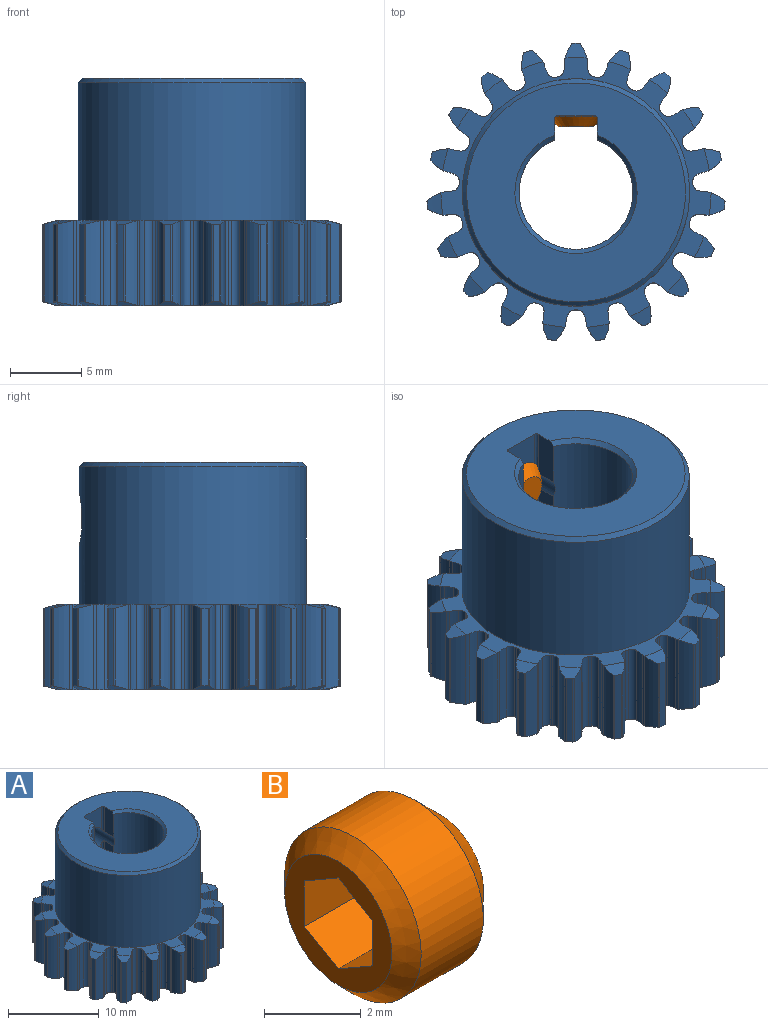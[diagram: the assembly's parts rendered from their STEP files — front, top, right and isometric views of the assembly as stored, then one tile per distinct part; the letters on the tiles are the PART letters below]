
ASSEMBLY  parts=2 mates=1
PART A: 286 faces, bbox 21x21x16 mm
  f0: plane 3.39x1.5mm, normal (-1,0,0), area 5mm2, adj f1,f3,f13,f14,f197
  f1: cone r=4mm half-angle=45deg, axis (0,0,1), area 9.8mm2, adj f0,f13,f14,f199
  f2: cylinder r=0.2mm len=11.39mm, axis (0,0,1), area 3.5mm2, adj f3,f11,f194,f200
  f3: cylinder r=1.62mm len=3.91mm, axis (0,-1,0), area 27mm2, adj f0,f2,f14,f194,f195,f196,f197,f198
  f4: cylinder r=3.17mm len=6mm, axis (0,0,1), area 6.3mm2, adj f5,f6,f150,f192
  f5: cylinder r=0.1mm len=5.49mm, axis (0,0,1), area 0.5mm2, adj f4,f6,f192,f250
  f6: cone r=9.5mm half-angle=75deg, axis (0,0,-1), area 1.1mm2, adj f4,f5,f10,f16,f250,f285
  f7: cylinder r=0.1mm len=5.49mm, axis (0,0,1), area 0.5mm2, adj f193,f221,f227,f242
  f8: cylinder r=3.17mm len=6mm, axis (0,0,1), area 6.3mm2, adj f9,f193,f221,f243
  f9: cylinder r=0.1mm len=5.49mm, axis (0,0,1), area 0.5mm2, adj f8,f193,f221,f227
  f10: cylinder r=0.1mm len=5.49mm, axis (0,0,1), area 0.5mm2, adj f6,f16,f192,f250
  f11: plane 19x18.97mm, normal (0,0,-1), area 192.8mm2, adj f2,f12,f18,f19,f20,f21,f22,f23
  f12: cone r=4.3mm half-angle=45deg, axis (0,0,-1), area 9.8mm2, adj f11,f14,f200,f201
  f13: plane 15.4x15.4mm, normal (0,0,1), area 124.6mm2, adj f0,f1,f196,f197,f199,f202,f203
  f14: cylinder r=4mm len=15.4mm, axis (0,0,1), area 339.5mm2, adj f0,f1,f3,f12,f199,f200,f201
  f15: cylinder r=8mm len=16mm, axis (0,0,1), area 476.3mm2, adj f195,f203,f285
  f16: cylinder r=3.17mm len=6mm, axis (0,0,1), area 6.3mm2, adj f6,f10,f192,f249
  f17: cylinder r=3.17mm len=6mm, axis (0,0,1), area 6.3mm2, adj f18,f153,f169,f218
  f18: cylinder r=0.81mm len=6mm, axis (0,0,1), area 1.6mm2, adj f11,f17,f19,f285
  f19: cylinder r=2.92mm len=6mm, axis (0,0,1), area 3.9mm2, adj f11,f18,f20,f285
  f20: cylinder r=0.5mm len=6mm, axis (0,0,1), area 3.7mm2, adj f11,f19,f21,f285
  f21: cylinder r=8.25mm len=6mm, axis (0,0,1), area 1.1mm2, adj f11,f20,f22,f285
  f22: cylinder r=0.5mm len=6mm, axis (0,0,1), area 3.7mm2, adj f11,f21,f23,f285
  f23: cylinder r=2.92mm len=6mm, axis (0,0,1), area 3.9mm2, adj f11,f22,f24,f285
  f24: cylinder r=0.81mm len=6mm, axis (0,0,1), area 1.6mm2, adj f11,f23,f25,f285
  f25: cylinder r=3.17mm len=6mm, axis (0,0,1), area 6.3mm2, adj f24,f170,f178,f217
  f26: cylinder r=3.17mm len=6mm, axis (0,0,1), area 6.3mm2, adj f27,f170,f176,f217
  f27: cylinder r=0.81mm len=6mm, axis (0,0,1), area 1.6mm2, adj f11,f26,f28,f285
  f28: cylinder r=2.92mm len=6mm, axis (0,0,1), area 3.9mm2, adj f11,f27,f29,f285
  f29: cylinder r=0.5mm len=6mm, axis (0,0,1), area 3.7mm2, adj f11,f28,f30,f285
  f30: cylinder r=8.25mm len=6mm, axis (0,0,1), area 1.1mm2, adj f11,f29,f31,f285
  f31: cylinder r=0.5mm len=6mm, axis (0,0,1), area 3.7mm2, adj f11,f30,f32,f285
  f32: cylinder r=2.92mm len=6mm, axis (0,0,1), area 3.9mm2, adj f11,f31,f33,f285
  f33: cylinder r=0.81mm len=6mm, axis (0,0,1), area 1.6mm2, adj f11,f32,f34,f285
  f34: cylinder r=3.17mm len=6mm, axis (0,0,1), area 6.3mm2, adj f33,f171,f175,f216
  f35: cylinder r=3.17mm len=6mm, axis (0,0,1), area 6.3mm2, adj f36,f171,f172,f216
  f36: cylinder r=0.81mm len=6mm, axis (0,0,1), area 1.6mm2, adj f11,f35,f37,f285
  f37: cylinder r=2.92mm len=6mm, axis (0,0,1), area 3.9mm2, adj f11,f36,f38,f285
  f38: cylinder r=0.5mm len=6mm, axis (0,0,1), area 3.7mm2, adj f11,f37,f39,f285
  f39: cylinder r=8.25mm len=6mm, axis (0,0,1), area 1.1mm2, adj f11,f38,f40,f285
  f40: cylinder r=0.5mm len=6mm, axis (0,0,1), area 3.7mm2, adj f11,f39,f41,f285
  f41: cylinder r=2.92mm len=6mm, axis (0,0,1), area 3.9mm2, adj f11,f40,f42,f285
  f42: cylinder r=0.81mm len=6mm, axis (0,0,1), area 1.6mm2, adj f11,f41,f43,f285
  f43: cylinder r=3.17mm len=6mm, axis (0,0,1), area 6.3mm2, adj f42,f173,f181,f215
  f44: cylinder r=3.17mm len=6mm, axis (0,0,1), area 6.3mm2, adj f45,f181,f215,f284
  f45: cylinder r=0.81mm len=6mm, axis (0,0,1), area 1.6mm2, adj f11,f44,f46,f285
  f46: cylinder r=2.92mm len=6mm, axis (0,0,1), area 3.9mm2, adj f11,f45,f47,f285
  f47: cylinder r=0.5mm len=6mm, axis (0,0,1), area 3.7mm2, adj f11,f46,f48,f285
  f48: cylinder r=8.25mm len=6mm, axis (0,0,1), area 1.1mm2, adj f11,f47,f49,f285
  f49: cylinder r=0.5mm len=6mm, axis (0,0,1), area 3.7mm2, adj f11,f48,f50,f285
  f50: cylinder r=2.92mm len=6mm, axis (0,0,1), area 3.9mm2, adj f11,f49,f51,f285
  f51: cylinder r=0.81mm len=6mm, axis (0,0,1), area 1.6mm2, adj f11,f50,f52,f285
  f52: cylinder r=3.17mm len=6mm, axis (0,0,1), area 6.3mm2, adj f51,f180,f214,f283
  f53: cylinder r=3.17mm len=6mm, axis (0,0,1), area 6.3mm2, adj f54,f180,f214,f281
  f54: cylinder r=0.81mm len=6mm, axis (0,0,1), area 1.6mm2, adj f11,f53,f55,f285
  f55: cylinder r=2.92mm len=6mm, axis (0,0,1), area 3.9mm2, adj f11,f54,f56,f285
  f56: cylinder r=0.5mm len=6mm, axis (0,0,1), area 3.7mm2, adj f11,f55,f57,f285
  f57: cylinder r=8.25mm len=6mm, axis (0,0,1), area 1.1mm2, adj f11,f56,f58,f285
  f58: cylinder r=0.5mm len=6mm, axis (0,0,1), area 3.7mm2, adj f11,f57,f59,f285
  f59: cylinder r=2.92mm len=6mm, axis (0,0,1), area 3.9mm2, adj f11,f58,f60,f285
  f60: cylinder r=0.81mm len=6mm, axis (0,0,1), area 1.6mm2, adj f11,f59,f61,f285
  f61: cylinder r=3.17mm len=6mm, axis (0,0,1), area 6.3mm2, adj f60,f182,f213,f280
  f62: cylinder r=3.17mm len=6mm, axis (0,0,1), area 6.3mm2, adj f63,f182,f213,f278
  f63: cylinder r=0.81mm len=6mm, axis (0,0,1), area 1.6mm2, adj f11,f62,f64,f285
  f64: cylinder r=2.92mm len=6mm, axis (0,0,1), area 3.9mm2, adj f11,f63,f65,f285
  f65: cylinder r=0.5mm len=6mm, axis (0,0,1), area 3.7mm2, adj f11,f64,f66,f285
  f66: cylinder r=8.25mm len=6mm, axis (0,0,1), area 1.1mm2, adj f11,f65,f67,f285
  f67: cylinder r=0.5mm len=6mm, axis (0,0,1), area 3.7mm2, adj f11,f66,f68,f285
  f68: cylinder r=2.92mm len=6mm, axis (0,0,1), area 3.9mm2, adj f11,f67,f69,f285
  f69: cylinder r=0.81mm len=6mm, axis (0,0,1), area 1.6mm2, adj f11,f68,f70,f285
  f70: cylinder r=3.17mm len=6mm, axis (0,0,1), area 6.3mm2, adj f69,f183,f212,f277
  f71: cylinder r=3.17mm len=6mm, axis (0,0,1), area 6.3mm2, adj f72,f183,f212,f275
  f72: cylinder r=0.81mm len=6mm, axis (0,0,1), area 1.6mm2, adj f11,f71,f73,f285
  f73: cylinder r=2.92mm len=6mm, axis (0,0,1), area 3.9mm2, adj f11,f72,f74,f285
  f74: cylinder r=0.5mm len=6mm, axis (0,0,1), area 3.7mm2, adj f11,f73,f75,f285
  f75: cylinder r=8.25mm len=6mm, axis (0,0,1), area 1.1mm2, adj f11,f74,f76,f285
  f76: cylinder r=0.5mm len=6mm, axis (0,0,1), area 3.7mm2, adj f11,f75,f77,f285
  f77: cylinder r=2.92mm len=6mm, axis (0,0,1), area 3.9mm2, adj f11,f76,f78,f285
  f78: cylinder r=0.81mm len=6mm, axis (0,0,1), area 1.6mm2, adj f11,f77,f79,f285
  f79: cylinder r=3.17mm len=6mm, axis (0,0,1), area 6.3mm2, adj f78,f184,f211,f274
  f80: cylinder r=3.17mm len=6mm, axis (0,0,1), area 6.3mm2, adj f81,f184,f211,f272
  f81: cylinder r=0.81mm len=6mm, axis (0,0,1), area 1.6mm2, adj f11,f80,f82,f285
  f82: cylinder r=2.92mm len=6mm, axis (0,0,1), area 3.9mm2, adj f11,f81,f83,f285
  f83: cylinder r=0.5mm len=6mm, axis (0,0,1), area 3.7mm2, adj f11,f82,f84,f285
  f84: cylinder r=8.25mm len=6mm, axis (0,0,1), area 1.1mm2, adj f11,f83,f85,f285
  f85: cylinder r=0.5mm len=6mm, axis (0,0,1), area 3.7mm2, adj f11,f84,f86,f285
  f86: cylinder r=2.92mm len=6mm, axis (0,0,1), area 3.9mm2, adj f11,f85,f87,f285
  f87: cylinder r=0.81mm len=6mm, axis (0,0,1), area 1.6mm2, adj f11,f86,f88,f285
  f88: cylinder r=3.17mm len=6mm, axis (0,0,1), area 6.3mm2, adj f87,f185,f210,f271
  f89: cylinder r=3.17mm len=6mm, axis (0,0,1), area 6.3mm2, adj f90,f185,f210,f269
  f90: cylinder r=0.81mm len=6mm, axis (0,0,1), area 1.6mm2, adj f11,f89,f91,f285
  f91: cylinder r=2.92mm len=6mm, axis (0,0,1), area 3.9mm2, adj f11,f90,f92,f285
  f92: cylinder r=0.5mm len=6mm, axis (0,0,1), area 3.7mm2, adj f11,f91,f93,f285
  f93: cylinder r=8.25mm len=6mm, axis (0,0,1), area 1.1mm2, adj f11,f92,f94,f285
  f94: cylinder r=0.5mm len=6mm, axis (0,0,1), area 3.7mm2, adj f11,f93,f95,f285
  f95: cylinder r=2.92mm len=6mm, axis (0,0,1), area 3.9mm2, adj f11,f94,f96,f285
  f96: cylinder r=0.81mm len=6mm, axis (0,0,1), area 1.6mm2, adj f11,f95,f97,f285
  f97: cylinder r=3.17mm len=6mm, axis (0,0,1), area 6.3mm2, adj f96,f186,f209,f268
  f98: cylinder r=3.17mm len=6mm, axis (0,0,1), area 6.3mm2, adj f99,f186,f209,f266
  f99: cylinder r=0.81mm len=6mm, axis (0,0,1), area 1.6mm2, adj f11,f98,f100,f285
  f100: cylinder r=2.92mm len=6mm, axis (0,0,1), area 3.9mm2, adj f11,f99,f101,f285
  f101: cylinder r=0.5mm len=6mm, axis (0,0,1), area 3.7mm2, adj f11,f100,f102,f285
  f102: cylinder r=8.25mm len=6mm, axis (0,0,1), area 1.1mm2, adj f11,f101,f103,f285
  f103: cylinder r=0.5mm len=6mm, axis (0,0,1), area 3.7mm2, adj f11,f102,f104,f285
  f104: cylinder r=2.92mm len=6mm, axis (0,0,1), area 3.9mm2, adj f11,f103,f105,f285
  f105: cylinder r=0.81mm len=6mm, axis (0,0,1), area 1.6mm2, adj f11,f104,f106,f285
  f106: cylinder r=3.17mm len=6mm, axis (0,0,1), area 6.3mm2, adj f105,f187,f208,f265
  f107: cylinder r=3.17mm len=6mm, axis (0,0,1), area 6.3mm2, adj f108,f187,f208,f263
  f108: cylinder r=0.81mm len=6mm, axis (0,0,1), area 1.6mm2, adj f11,f107,f109,f285
  f109: cylinder r=2.92mm len=6mm, axis (0,0,1), area 3.9mm2, adj f11,f108,f110,f285
  f110: cylinder r=0.5mm len=6mm, axis (0,0,1), area 3.7mm2, adj f11,f109,f111,f285
  f111: cylinder r=8.25mm len=6mm, axis (0,0,1), area 1.1mm2, adj f11,f110,f112,f285
  f112: cylinder r=0.5mm len=6mm, axis (0,0,1), area 3.7mm2, adj f11,f111,f113,f285
  f113: cylinder r=2.92mm len=6mm, axis (0,0,1), area 3.9mm2, adj f11,f112,f114,f285
  f114: cylinder r=0.81mm len=6mm, axis (0,0,1), area 1.6mm2, adj f11,f113,f115,f285
  f115: cylinder r=3.17mm len=6mm, axis (0,0,1), area 6.3mm2, adj f114,f188,f207,f262
  f116: cylinder r=3.17mm len=6mm, axis (0,0,1), area 6.3mm2, adj f117,f188,f207,f260
  f117: cylinder r=0.81mm len=6mm, axis (0,0,1), area 1.6mm2, adj f11,f116,f118,f285
  f118: cylinder r=2.92mm len=6mm, axis (0,0,1), area 3.9mm2, adj f11,f117,f119,f285
  f119: cylinder r=0.5mm len=6mm, axis (0,0,1), area 3.7mm2, adj f11,f118,f120,f285
  f120: cylinder r=8.25mm len=6mm, axis (0,0,1), area 1.1mm2, adj f11,f119,f121,f285
  f121: cylinder r=0.5mm len=6mm, axis (0,0,1), area 3.7mm2, adj f11,f120,f122,f285
  f122: cylinder r=2.92mm len=6mm, axis (0,0,1), area 3.9mm2, adj f11,f121,f123,f285
  f123: cylinder r=0.81mm len=6mm, axis (0,0,1), area 1.6mm2, adj f11,f122,f124,f285
  f124: cylinder r=3.17mm len=6mm, axis (0,0,1), area 6.3mm2, adj f123,f189,f206,f259
  f125: cylinder r=3.17mm len=6mm, axis (0,0,1), area 6.3mm2, adj f126,f189,f206,f257
  f126: cylinder r=0.81mm len=6mm, axis (0,0,1), area 1.6mm2, adj f11,f125,f127,f285
  f127: cylinder r=2.92mm len=6mm, axis (0,0,1), area 3.9mm2, adj f11,f126,f128,f285
  f128: cylinder r=0.5mm len=6mm, axis (0,0,1), area 3.7mm2, adj f11,f127,f129,f285
  f129: cylinder r=8.25mm len=6mm, axis (0,0,1), area 1.1mm2, adj f11,f128,f130,f285
  f130: cylinder r=0.5mm len=6mm, axis (0,0,1), area 3.7mm2, adj f11,f129,f131,f285
  f131: cylinder r=2.92mm len=6mm, axis (0,0,1), area 3.9mm2, adj f11,f130,f132,f285
  f132: cylinder r=0.81mm len=6mm, axis (0,0,1), area 1.6mm2, adj f11,f131,f133,f285
  f133: cylinder r=3.17mm len=6mm, axis (0,0,1), area 6.3mm2, adj f132,f190,f205,f256
  f134: cylinder r=3.17mm len=6mm, axis (0,0,1), area 6.3mm2, adj f135,f190,f205,f254
  f135: cylinder r=0.81mm len=6mm, axis (0,0,1), area 1.6mm2, adj f11,f134,f136,f285
  f136: cylinder r=2.92mm len=6mm, axis (0,0,1), area 3.9mm2, adj f11,f135,f137,f285
  f137: cylinder r=0.5mm len=6mm, axis (0,0,1), area 3.7mm2, adj f11,f136,f138,f285
  f138: cylinder r=8.25mm len=6mm, axis (0,0,1), area 1.1mm2, adj f11,f137,f139,f285
  f139: cylinder r=0.5mm len=6mm, axis (0,0,1), area 3.7mm2, adj f11,f138,f140,f285
  f140: cylinder r=2.92mm len=6mm, axis (0,0,1), area 3.9mm2, adj f11,f139,f141,f285
  f141: cylinder r=0.81mm len=6mm, axis (0,0,1), area 1.6mm2, adj f11,f140,f142,f285
  f142: cylinder r=3.17mm len=6mm, axis (0,0,1), area 6.3mm2, adj f141,f191,f204,f253
  f143: cylinder r=3.17mm len=6mm, axis (0,0,1), area 6.3mm2, adj f144,f191,f204,f251
  f144: cylinder r=0.81mm len=6mm, axis (0,0,1), area 1.6mm2, adj f11,f143,f145,f285
  f145: cylinder r=2.92mm len=6mm, axis (0,0,1), area 3.9mm2, adj f11,f144,f146,f285
  f146: cylinder r=0.5mm len=6mm, axis (0,0,1), area 3.7mm2, adj f11,f145,f147,f285
  f147: cylinder r=8.25mm len=6mm, axis (0,0,1), area 1.1mm2, adj f11,f146,f148,f285
  f148: cylinder r=0.5mm len=6mm, axis (0,0,1), area 3.7mm2, adj f11,f147,f149,f285
  f149: cylinder r=2.92mm len=6mm, axis (0,0,1), area 3.9mm2, adj f11,f148,f150,f285
  f150: cylinder r=0.81mm len=6mm, axis (0,0,1), area 1.6mm2, adj f4,f11,f149,f285
  f151: cylinder r=0.1mm len=5.49mm, axis (0,0,1), area 0.5mm2, adj f152,f162,f169,f218
  f152: cylinder r=10.5mm len=5.46mm, axis (0,0,1), area 2.6mm2, adj f151,f153,f169,f218
  f153: cylinder r=0.1mm len=5.49mm, axis (0,0,1), area 0.5mm2, adj f17,f152,f169,f218
  f154: cylinder r=3.17mm len=6mm, axis (0,0,1), area 6.3mm2, adj f155,f167,f219,f226
  f155: cylinder r=0.81mm len=6mm, axis (0,0,1), area 1.6mm2, adj f11,f154,f156,f285
  f156: cylinder r=2.92mm len=6mm, axis (0,0,1), area 3.9mm2, adj f11,f155,f157,f285
  f157: cylinder r=0.5mm len=6mm, axis (0,0,1), area 3.7mm2, adj f11,f156,f158,f285
  f158: cylinder r=8.25mm len=6mm, axis (0,0,1), area 1.1mm2, adj f11,f157,f159,f285
  f159: cylinder r=0.5mm len=6mm, axis (0,0,1), area 3.7mm2, adj f11,f158,f160,f285
  f160: cylinder r=2.92mm len=6mm, axis (0,0,1), area 3.9mm2, adj f11,f159,f161,f285
  f161: cylinder r=0.81mm len=6mm, axis (0,0,1), area 1.6mm2, adj f11,f160,f162,f285
  f162: cylinder r=3.17mm len=6mm, axis (0,0,1), area 6.3mm2, adj f151,f161,f169,f218
  f163: cylinder r=3.17mm len=6mm, axis (0,0,1), area 6.3mm2, adj f164,f167,f219,f229
  f164: cylinder r=0.1mm len=5.49mm, axis (0,0,1), area 0.5mm2, adj f163,f167,f219,f225
  f165: cylinder r=0.1mm len=5.49mm, axis (0,0,1), area 0.5mm2, adj f166,f168,f220,f224
  f166: cylinder r=3.17mm len=6mm, axis (0,0,1), area 6.3mm2, adj f165,f168,f220,f234
  f167: cone r=15.5mm half-angle=75deg, axis (0,0,1), area 1.1mm2, adj f11,f154,f163,f164,f225,f226
  f168: cone r=15.5mm half-angle=75deg, axis (0,0,1), area 1.1mm2, adj f11,f165,f166,f222,f223,f224
  f169: cone r=15.5mm half-angle=75deg, axis (0,0,1), area 1.1mm2, adj f11,f17,f151,f152,f153,f162
  f170: cone r=15.5mm half-angle=75deg, axis (0,0,1), area 1.1mm2, adj f11,f25,f26,f176,f177,f178
  f171: cone r=15.5mm half-angle=75deg, axis (0,0,1), area 1.1mm2, adj f11,f34,f35,f172,f174,f175
  f172: cylinder r=0.1mm len=5.49mm, axis (0,0,1), area 0.5mm2, adj f35,f171,f174,f216
  f173: cylinder r=0.1mm len=5.49mm, axis (0,0,1), area 0.5mm2, adj f43,f179,f181,f215
  f174: cylinder r=10.5mm len=5.46mm, axis (0,0,1), area 2.6mm2, adj f171,f172,f175,f216
  f175: cylinder r=0.1mm len=5.49mm, axis (0,0,1), area 0.5mm2, adj f34,f171,f174,f216
  f176: cylinder r=0.1mm len=5.49mm, axis (0,0,1), area 0.5mm2, adj f26,f170,f177,f217
  f177: cylinder r=10.5mm len=5.46mm, axis (0,0,1), area 2.6mm2, adj f170,f176,f178,f217
  f178: cylinder r=0.1mm len=5.49mm, axis (0,0,1), area 0.5mm2, adj f25,f170,f177,f217
  f179: cylinder r=10.5mm len=5.46mm, axis (0,0,1), area 2.6mm2, adj f173,f181,f215,f284
  f180: cone r=15.5mm half-angle=75deg, axis (0,0,1), area 1.1mm2, adj f11,f52,f53,f281,f282,f283
  f181: cone r=15.5mm half-angle=75deg, axis (0,0,1), area 1.1mm2, adj f11,f43,f44,f173,f179,f284
  f182: cone r=15.5mm half-angle=75deg, axis (0,0,1), area 1.1mm2, adj f11,f61,f62,f278,f279,f280
  f183: cone r=15.5mm half-angle=75deg, axis (0,0,1), area 1.1mm2, adj f11,f70,f71,f275,f276,f277
  f184: cone r=15.5mm half-angle=75deg, axis (0,0,1), area 1.1mm2, adj f11,f79,f80,f272,f273,f274
  f185: cone r=15.5mm half-angle=75deg, axis (0,0,1), area 1.1mm2, adj f11,f88,f89,f269,f270,f271
  f186: cone r=15.5mm half-angle=75deg, axis (0,0,1), area 1.1mm2, adj f11,f97,f98,f266,f267,f268
  f187: cone r=15.5mm half-angle=75deg, axis (0,0,1), area 1.1mm2, adj f11,f106,f107,f263,f264,f265
  f188: cone r=15.5mm half-angle=75deg, axis (0,0,1), area 1.1mm2, adj f11,f115,f116,f260,f261,f262
  f189: cone r=15.5mm half-angle=75deg, axis (0,0,1), area 1.1mm2, adj f11,f124,f125,f257,f258,f259
  f190: cone r=15.5mm half-angle=75deg, axis (0,0,1), area 1.1mm2, adj f11,f133,f134,f254,f255,f256
  f191: cone r=15.5mm half-angle=75deg, axis (0,0,1), area 1.1mm2, adj f11,f142,f143,f251,f252,f253
  f192: cone r=15.5mm half-angle=75deg, axis (0,0,1), area 1.1mm2, adj f4,f5,f10,f11,f16,f250
  f193: cone r=15.5mm half-angle=75deg, axis (0,0,1), area 1.1mm2, adj f7,f8,f9,f11,f227,f242
  f194: plane 11.03x2.6mm, normal (0,-1,0), area 27.5mm2, adj f2,f3,f11,f198
  f195: cone r=1.62mm half-angle=45deg, axis (0,1,0), area 5.1mm2, adj f3,f15
  f196: plane 3.03x2.6mm, normal (0,-1,0), area 6.7mm2, adj f3,f13,f197,f202
  f197: cylinder r=0.2mm len=3.39mm, axis (0,0,1), area 1mm2, adj f0,f3,f13,f196
  f198: cylinder r=0.2mm len=11.39mm, axis (0,0,1), area 3.5mm2, adj f3,f11,f194,f201
  f199: plane 3.39x1.5mm, normal (1,0,0), area 5mm2, adj f1,f3,f13,f14,f202
  f200: plane 11.39x1.5mm, normal (1,0,0), area 16.9mm2, adj f2,f3,f11,f12,f14
  f201: plane 11.39x1.5mm, normal (-1,0,0), area 16.9mm2, adj f3,f11,f12,f14,f198
  f202: cylinder r=0.2mm len=3.39mm, axis (0,0,1), area 1mm2, adj f3,f13,f196,f199
  f203: cone r=7.7mm half-angle=45deg, axis (0,0,-1), area 20.9mm2, adj f13,f15
  f204: cone r=9.5mm half-angle=75deg, axis (0,0,-1), area 1.1mm2, adj f142,f143,f251,f252,f253,f285
  f205: cone r=9.5mm half-angle=75deg, axis (0,0,-1), area 1.1mm2, adj f133,f134,f254,f255,f256,f285
  f206: cone r=9.5mm half-angle=75deg, axis (0,0,-1), area 1.1mm2, adj f124,f125,f257,f258,f259,f285
  f207: cone r=9.5mm half-angle=75deg, axis (0,0,-1), area 1.1mm2, adj f115,f116,f260,f261,f262,f285
  f208: cone r=9.5mm half-angle=75deg, axis (0,0,-1), area 1.1mm2, adj f106,f107,f263,f264,f265,f285
  f209: cone r=9.5mm half-angle=75deg, axis (0,0,-1), area 1.1mm2, adj f97,f98,f266,f267,f268,f285
  f210: cone r=9.5mm half-angle=75deg, axis (0,0,-1), area 1.1mm2, adj f88,f89,f269,f270,f271,f285
  f211: cone r=9.5mm half-angle=75deg, axis (0,0,-1), area 1.1mm2, adj f79,f80,f272,f273,f274,f285
  f212: cone r=9.5mm half-angle=75deg, axis (0,0,-1), area 1.1mm2, adj f70,f71,f275,f276,f277,f285
  f213: cone r=9.5mm half-angle=75deg, axis (0,0,-1), area 1.1mm2, adj f61,f62,f278,f279,f280,f285
  f214: cone r=9.5mm half-angle=75deg, axis (0,0,-1), area 1.1mm2, adj f52,f53,f281,f282,f283,f285
  f215: cone r=9.5mm half-angle=75deg, axis (0,0,-1), area 1.1mm2, adj f43,f44,f173,f179,f284,f285
  f216: cone r=9.5mm half-angle=75deg, axis (0,0,-1), area 1.1mm2, adj f34,f35,f172,f174,f175,f285
  f217: cone r=9.5mm half-angle=75deg, axis (0,0,-1), area 1.1mm2, adj f25,f26,f176,f177,f178,f285
  f218: cone r=9.5mm half-angle=75deg, axis (0,0,-1), area 1.1mm2, adj f17,f151,f152,f153,f162,f285
  f219: cone r=9.5mm half-angle=75deg, axis (0,0,-1), area 1.1mm2, adj f154,f163,f164,f225,f226,f285
  f220: cone r=9.5mm half-angle=75deg, axis (0,0,-1), area 1.1mm2, adj f165,f166,f222,f223,f224,f285
  f221: cone r=9.5mm half-angle=75deg, axis (0,0,-1), area 1.1mm2, adj f7,f8,f9,f227,f242,f285
  f222: cylinder r=3.17mm len=6mm, axis (0,0,1), area 6.3mm2, adj f168,f220,f223,f235
  f223: cylinder r=0.1mm len=5.49mm, axis (0,0,1), area 0.5mm2, adj f168,f220,f222,f224
  f224: cylinder r=10.5mm len=5.46mm, axis (0,0,1), area 2.6mm2, adj f165,f168,f220,f223
  f225: cylinder r=10.5mm len=5.46mm, axis (0,0,1), area 2.6mm2, adj f164,f167,f219,f226
  f226: cylinder r=0.1mm len=5.49mm, axis (0,0,1), area 0.5mm2, adj f154,f167,f219,f225
  f227: cylinder r=10.5mm len=5.46mm, axis (0,0,1), area 2.6mm2, adj f7,f9,f193,f221
  f228: cylinder r=2.92mm len=6mm, axis (0,0,1), area 3.9mm2, adj f11,f229,f230,f285
  f229: cylinder r=0.81mm len=6mm, axis (0,0,1), area 1.6mm2, adj f11,f163,f228,f285
  f230: cylinder r=0.5mm len=6mm, axis (0,0,1), area 3.7mm2, adj f11,f228,f231,f285
  f231: cylinder r=8.25mm len=6mm, axis (0,0,1), area 1.1mm2, adj f11,f230,f232,f285
  f232: cylinder r=0.5mm len=6mm, axis (0,0,1), area 3.7mm2, adj f11,f231,f233,f285
  f233: cylinder r=2.92mm len=6mm, axis (0,0,1), area 3.9mm2, adj f11,f232,f234,f285
  f234: cylinder r=0.81mm len=6mm, axis (0,0,1), area 1.6mm2, adj f11,f166,f233,f285
  f235: cylinder r=0.81mm len=6mm, axis (0,0,1), area 1.6mm2, adj f11,f222,f236,f285
  f236: cylinder r=2.92mm len=6mm, axis (0,0,1), area 3.9mm2, adj f11,f235,f237,f285
  f237: cylinder r=0.5mm len=6mm, axis (0,0,1), area 3.7mm2, adj f11,f236,f238,f285
  f238: cylinder r=8.25mm len=6mm, axis (0,0,1), area 1.1mm2, adj f11,f237,f239,f285
  f239: cylinder r=0.5mm len=6mm, axis (0,0,1), area 3.7mm2, adj f11,f238,f240,f285
  f240: cylinder r=2.92mm len=6mm, axis (0,0,1), area 3.9mm2, adj f11,f239,f241,f285
  f241: cylinder r=0.81mm len=6mm, axis (0,0,1), area 1.6mm2, adj f11,f240,f242,f285
  f242: cylinder r=3.17mm len=6mm, axis (0,0,1), area 6.3mm2, adj f7,f193,f221,f241
  f243: cylinder r=0.81mm len=6mm, axis (0,0,1), area 1.6mm2, adj f8,f11,f244,f285
  f244: cylinder r=2.92mm len=6mm, axis (0,0,1), area 3.9mm2, adj f11,f243,f245,f285
  f245: cylinder r=0.5mm len=6mm, axis (0,0,1), area 3.7mm2, adj f11,f244,f246,f285
  f246: cylinder r=8.25mm len=6mm, axis (0,0,1), area 1.1mm2, adj f11,f245,f247,f285
  f247: cylinder r=0.5mm len=6mm, axis (0,0,1), area 3.7mm2, adj f11,f246,f248,f285
  f248: cylinder r=2.92mm len=6mm, axis (0,0,1), area 3.9mm2, adj f11,f247,f249,f285
  f249: cylinder r=0.81mm len=6mm, axis (0,0,1), area 1.6mm2, adj f11,f16,f248,f285
  f250: cylinder r=10.5mm len=5.46mm, axis (0,0,1), area 2.6mm2, adj f5,f6,f10,f192
  f251: cylinder r=0.1mm len=5.49mm, axis (0,0,1), area 0.5mm2, adj f143,f191,f204,f252
  f252: cylinder r=10.5mm len=5.46mm, axis (0,0,1), area 2.6mm2, adj f191,f204,f251,f253
  f253: cylinder r=0.1mm len=5.49mm, axis (0,0,1), area 0.5mm2, adj f142,f191,f204,f252
  f254: cylinder r=0.1mm len=5.49mm, axis (0,0,1), area 0.5mm2, adj f134,f190,f205,f255
  f255: cylinder r=10.5mm len=5.46mm, axis (0,0,1), area 2.6mm2, adj f190,f205,f254,f256
  f256: cylinder r=0.1mm len=5.49mm, axis (0,0,1), area 0.5mm2, adj f133,f190,f205,f255
  f257: cylinder r=0.1mm len=5.49mm, axis (0,0,1), area 0.5mm2, adj f125,f189,f206,f258
  f258: cylinder r=10.5mm len=5.46mm, axis (0,0,1), area 2.6mm2, adj f189,f206,f257,f259
  f259: cylinder r=0.1mm len=5.49mm, axis (0,0,1), area 0.5mm2, adj f124,f189,f206,f258
  f260: cylinder r=0.1mm len=5.49mm, axis (0,0,1), area 0.5mm2, adj f116,f188,f207,f261
  f261: cylinder r=10.5mm len=5.46mm, axis (0,0,1), area 2.6mm2, adj f188,f207,f260,f262
  f262: cylinder r=0.1mm len=5.49mm, axis (0,0,1), area 0.5mm2, adj f115,f188,f207,f261
  f263: cylinder r=0.1mm len=5.49mm, axis (0,0,1), area 0.5mm2, adj f107,f187,f208,f264
  f264: cylinder r=10.5mm len=5.46mm, axis (0,0,1), area 2.6mm2, adj f187,f208,f263,f265
  f265: cylinder r=0.1mm len=5.49mm, axis (0,0,1), area 0.5mm2, adj f106,f187,f208,f264
  f266: cylinder r=0.1mm len=5.49mm, axis (0,0,1), area 0.5mm2, adj f98,f186,f209,f267
  f267: cylinder r=10.5mm len=5.46mm, axis (0,0,1), area 2.6mm2, adj f186,f209,f266,f268
  f268: cylinder r=0.1mm len=5.49mm, axis (0,0,1), area 0.5mm2, adj f97,f186,f209,f267
  f269: cylinder r=0.1mm len=5.49mm, axis (0,0,1), area 0.5mm2, adj f89,f185,f210,f270
  f270: cylinder r=10.5mm len=5.46mm, axis (0,0,1), area 2.6mm2, adj f185,f210,f269,f271
  f271: cylinder r=0.1mm len=5.49mm, axis (0,0,1), area 0.5mm2, adj f88,f185,f210,f270
  f272: cylinder r=0.1mm len=5.49mm, axis (0,0,1), area 0.5mm2, adj f80,f184,f211,f273
  f273: cylinder r=10.5mm len=5.46mm, axis (0,0,1), area 2.6mm2, adj f184,f211,f272,f274
  f274: cylinder r=0.1mm len=5.49mm, axis (0,0,1), area 0.5mm2, adj f79,f184,f211,f273
  f275: cylinder r=0.1mm len=5.49mm, axis (0,0,1), area 0.5mm2, adj f71,f183,f212,f276
  f276: cylinder r=10.5mm len=5.46mm, axis (0,0,1), area 2.6mm2, adj f183,f212,f275,f277
  f277: cylinder r=0.1mm len=5.49mm, axis (0,0,1), area 0.5mm2, adj f70,f183,f212,f276
  f278: cylinder r=0.1mm len=5.49mm, axis (0,0,1), area 0.5mm2, adj f62,f182,f213,f279
  f279: cylinder r=10.5mm len=5.46mm, axis (0,0,1), area 2.6mm2, adj f182,f213,f278,f280
  f280: cylinder r=0.1mm len=5.49mm, axis (0,0,1), area 0.5mm2, adj f61,f182,f213,f279
  f281: cylinder r=0.1mm len=5.49mm, axis (0,0,1), area 0.5mm2, adj f53,f180,f214,f282
  f282: cylinder r=10.5mm len=5.46mm, axis (0,0,1), area 2.6mm2, adj f180,f214,f281,f283
  f283: cylinder r=0.1mm len=5.49mm, axis (0,0,1), area 0.5mm2, adj f52,f180,f214,f282
  f284: cylinder r=0.1mm len=5.49mm, axis (0,0,1), area 0.5mm2, adj f44,f179,f181,f215
  f285: plane 19x18.97mm, normal (0,0,1), area 53.4mm2, adj f6,f15,f18,f19,f20,f21,f22,f23
PART B: 18 faces, bbox 3x4x4 mm
  f0: plane 1x0.29mm, normal (-1,0,0), area 0.1mm2, adj f5,f6,f17
  f1: plane 0.87x0.5mm, normal (-1,0,0), area 0.1mm2, adj f5,f16,f17
  f2: plane 0.87x0.5mm, normal (-1,0,0), area 0.1mm2, adj f5,f6,f13
  f3: plane 0.87x0.5mm, normal (-1,0,0), area 0.1mm2, adj f5,f13,f14
  f4: plane 1x0.29mm, normal (-1,0,0), area 0.1mm2, adj f5,f14,f15
  f5: cone r=1mm half-angle=60deg, axis (-1,0,0), area 3.6mm2, adj f0,f1,f2,f3,f4,f7
  f6: plane 1.5x1mm, normal (0,0.5,0.87), area 1.7mm2, adj f0,f2,f8,f13,f17
  f7: plane 0.87x0.5mm, normal (-1,0,0), area 0.1mm2, adj f5,f15,f16
  f8: plane 3.14x3.14mm, normal (-1,0,0), area 4.3mm2, adj f6,f9,f13,f14,f15,f16,f17
  f9: cone r=1.57mm half-angle=45deg, axis (1,0,0), area 6.8mm2, adj f8,f10
  f10: cylinder r=2mm len=4mm, axis (-1,0,0), area 22.9mm2, adj f9,f11
  f11: cone r=2mm half-angle=45deg, axis (-1,0,0), area 10.8mm2, adj f10,f12
  f12: plane 2.5x2.5mm, normal (1,0,0), area 4.9mm2, adj f11
  f13: plane 1.5x1.15mm, normal (0,1,0), area 1.7mm2, adj f2,f3,f6,f8,f14
  f14: plane 1.5x1mm, normal (0,0.5,-0.87), area 1.7mm2, adj f3,f4,f8,f13,f15
  f15: plane 1.5x1mm, normal (0,-0.5,-0.87), area 1.7mm2, adj f4,f7,f8,f14,f16
  f16: plane 1.5x1.15mm, normal (0,-1,0), area 1.7mm2, adj f1,f7,f8,f15,f17
  f17: plane 1.5x1mm, normal (0,-0.5,0.87), area 1.7mm2, adj f0,f1,f6,f8,f16
PLACE A at identity
PLACE B rot(axis=(0.58,-0.58,-0.58),120deg) t=(0,4.62,12)mm
MATE fastened B.f5 <-> A.f3  axis (0,1,0) through (0,7.62,12)mm
